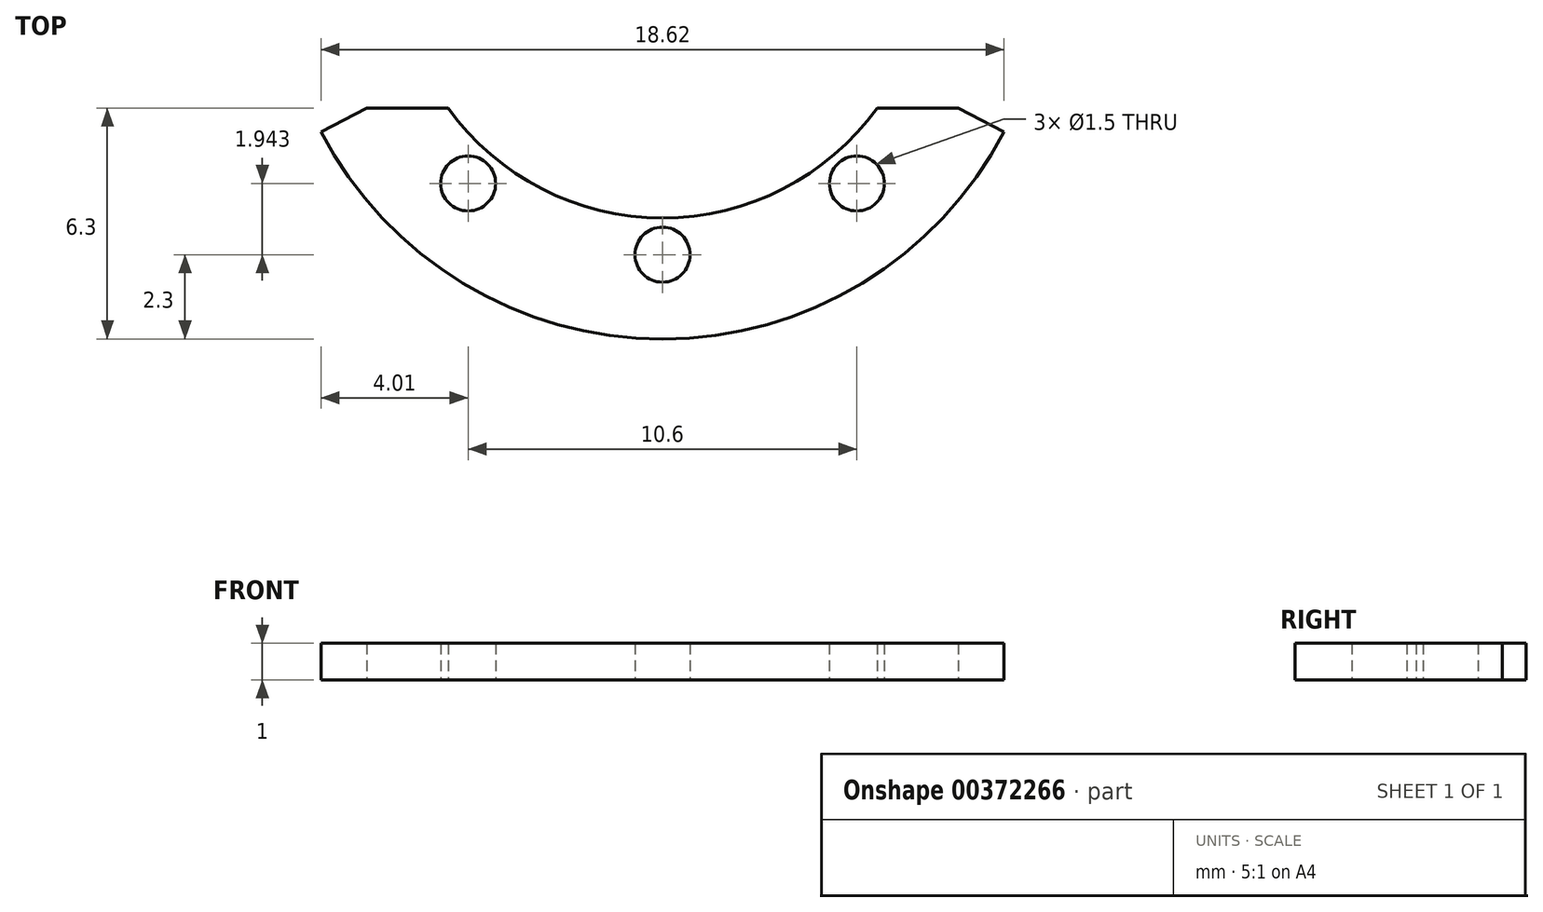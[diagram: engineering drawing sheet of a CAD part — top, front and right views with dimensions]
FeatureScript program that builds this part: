
annotation { "Feature Type Name" : "Feature", "Feature Type Description" : "" }
export const myFeature = defineFeature(function(context is Context, id is Id, definition is map)
    precondition{}
    {
        {
            var Q0;
            Q0=qCreatedBy(makeId("Top.planeOp"),FACE);
            var sketch = newSketch(context, id + "F0", { "sketchPlane" : qUnion([Q0])});
            skArc(sketch, "E0", {"start": v(-9.31, -4.85) * mm, "mid": v(0, -10.5) * mm, "end": v(9.31, -4.85) * mm});
            skLineSegment(sketch, "E1", {"start": v(-8.07, -4.2) * mm, "end": v(-5.85, -4.2) * mm});
            skLineSegment(sketch, "E2", {"start": v(-8.07, -4.2) * mm, "end": v(-9.31, -4.85) * mm});
            skLineSegment(sketch, "E3", {"start": v(8.07, -4.2) * mm, "end": v(9.31, -4.85) * mm});
            skArc(sketch, "E4", {"start": v(-7.27, -3.79) * mm, "mid": v(0, -8.2) * mm, "end": v(7.27, -3.79) * mm, "construction": true});
            skArc(sketch, "E5", {"start": v(-5.85, -4.2) * mm, "mid": v(0, -7.2) * mm, "end": v(5.85, -4.2) * mm});
            skCircle(sketch, "E6", {"center": v(-5.3, -6.26) * mm, "radius": 0.75 * mm});
            skCircle(sketch, "E7", {"center": v(0, -8.2) * mm, "radius": 0.75 * mm});
            skCircle(sketch, "E8", {"center": v(5.3, -6.26) * mm, "radius": 0.75 * mm});
            skLineSegment(sketch, "E9.trimOffspring", {"start": v(5.85, -4.2) * mm, "end": v(8.07, -4.2) * mm});
            skSolve(sketch);
        }
        {
            var Q0;
            Q0=makeQuery(id+"F0.imprint","IMPRINT",FACE,{"disambiguationData":[TD([[makeQuery(id+"F0.imprint","IMPRINT",EDGE,{"derivedFrom":sQuery(id+"F0.wireOp",EDGE,"E0")}),1.0]])]});
            extrude(context, id + "F1", {"entities" : qUnion([Q0]), "depth" : 1 * mm});
        }
    });
